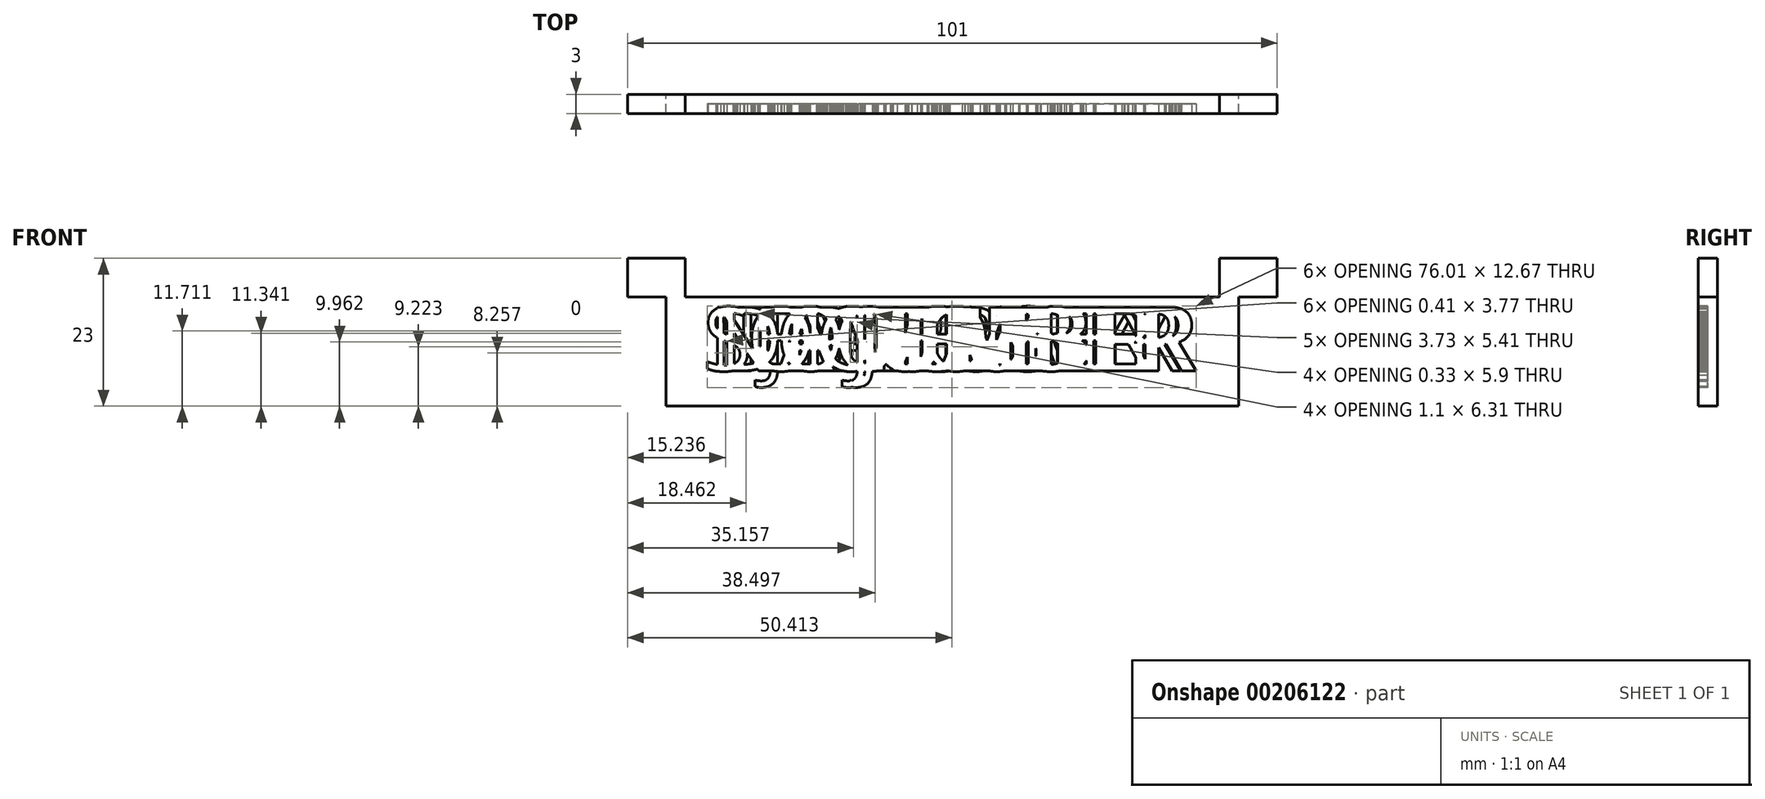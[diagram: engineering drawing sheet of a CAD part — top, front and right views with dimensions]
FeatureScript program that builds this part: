
annotation { "Feature Type Name" : "Feature", "Feature Type Description" : "" }
export const myFeature = defineFeature(function(context is Context, id is Id, definition is map)
    precondition{}
    {
        {
            var Q0;
            Q0=qCreatedBy(makeId("Front.planeOp"),FACE);
            var sketch = newSketch(context, id + "F0", { "sketchPlane" : qUnion([Q0])});
            skLineSegment(sketch, "E0.bottom", {"start": v(-51.5, 23) * mm, "end": v(-42.5, 23) * mm});
            skLineSegment(sketch, "E0.top", {"start": v(-45.5, 0) * mm, "end": v(43.5, 0) * mm});
            skLineSegment(sketch, "E0.left", {"start": v(-51.5, 23) * mm, "end": v(-51.5, 17) * mm});
            skLineSegment(sketch, "E0.right", {"start": v(49.5, 23) * mm, "end": v(49.5, 17) * mm});
            skLineSegment(sketch, "E1.top", {"start": v(-51.5, 17) * mm, "end": v(-45.5, 17) * mm});
            skLineSegment(sketch, "E1.right", {"start": v(-45.5, 0) * mm, "end": v(-45.5, 17) * mm});
            skLineSegment(sketch, "E2.bottom", {"start": v(-51.5, 23) * mm, "end": v(-42.5, 23) * mm, "construction": true});
            skLineSegment(sketch, "E2.top", {"start": v(-51.5, 17) * mm, "end": v(-42.5, 17) * mm, "construction": true});
            skLineSegment(sketch, "E2.left", {"start": v(-51.5, 23) * mm, "end": v(-51.5, 17) * mm, "construction": true});
            skLineSegment(sketch, "E2.right", {"start": v(-42.5, 23) * mm, "end": v(-42.5, 17) * mm, "construction": true});
            skLineSegment(sketch, "E3.top", {"start": v(-42.5, 17) * mm, "end": v(40.5, 17) * mm});
            skLineSegment(sketch, "E3.left", {"start": v(-42.5, 23) * mm, "end": v(-42.5, 17) * mm});
            skLineSegment(sketch, "E3.right", {"start": v(40.5, 23) * mm, "end": v(40.5, 17) * mm});
            skLineSegment(sketch, "E4.top", {"start": v(49.5, 17) * mm, "end": v(43.5, 17) * mm});
            skLineSegment(sketch, "E4.right", {"start": v(43.5, 0) * mm, "end": v(43.5, 17) * mm});
            skLineSegment(sketch, "E5.trimOffspring", {"start": v(40.5, 23) * mm, "end": v(49.5, 23) * mm});
            skSolve(sketch);
        }
        {
            var Q0;
            Q0=makeQuery(id+"F0.imprint","IMPRINT",FACE,{"disambiguationData":[TD([[makeQuery(id+"F0.imprint","IMPRINT",EDGE,{"derivedFrom":sQuery(id+"F0.wireOp",EDGE,"E0.bottom")}),-1.0]])]});
            extrude(context, id + "F1", {"entities" : qUnion([Q0]), "depth" : 3 * mm});
        }
        {
            var Q0;
            Q0=makeQuery(id+"F1.opExtrude","CAP_FACE",FACE,{"disambiguationData":[OSD([sQuery(id+"F0.wireOp",EDGE,"E0.bottom"),sQuery(id+"F0.wireOp",EDGE,"E0.top"),sQuery(id+"F0.wireOp",EDGE,"E0.left"),sQuery(id+"F0.wireOp",EDGE,"E0.right"),sQuery(id+"F0.wireOp",EDGE,"E1.top"),sQuery(id+"F0.wireOp",EDGE,"E1.right"),sQuery(id+"F0.wireOp",EDGE,"E3.top"),sQuery(id+"F0.wireOp",EDGE,"E3.left"),sQuery(id+"F0.wireOp",EDGE,"E3.right"),sQuery(id+"F0.wireOp",EDGE,"E4.top"),sQuery(id+"F0.wireOp",EDGE,"E4.right"),sQuery(id+"F0.wireOp",EDGE,"E5.trimOffspring")])],"isStart":false});
            var sketch = newSketch(context, id + "F2", { "sketchPlane" : qUnion([Q0])});
            skLineSegment(sketch, "E6.0", {"start": v(-45.5, 3.5) * mm, "end": v(-42, 3.5) * mm, "construction": true});
            skLineSegment(sketch, "E7.0", {"start": v(-42, 15.5) * mm, "end": v(40, 15.5) * mm, "construction": true});
            skLineSegment(sketch, "E8.0", {"start": v(-42, 0) * mm, "end": v(-42, 15.5) * mm, "construction": true});
            skText(sketch, "E9", { "text": "JANUARY", "fontName": "OpenSans-Regular.ttf"});
            skLineSegment(sketch, "E10.top", {"start": v(-45.5, 0) * mm, "end": v(-42, 0) * mm, "construction": true});
            skLineSegment(sketch, "E10.left", {"start": v(-45.5, 3.5) * mm, "end": v(-45.5, 0) * mm, "construction": true});
            skLineSegment(sketch, "E10.right", {"start": v(-42, 3.5) * mm, "end": v(-42, 0) * mm, "construction": true});
            skLineSegment(sketch, "E11.0", {"start": v(40, 0) * mm, "end": v(40, 17) * mm, "construction": true});
            skPoint(sketch, "E12.orphan", {"position": v(40, 15.5) * mm});
            skPoint(sketch, "E13.end.orphan", {"position": v(-1, 0) * mm});
            skLineSegment(sketch, "E14", {"start": v(-1, 17) * mm, "end": v(-1, 0) * mm, "construction": true});
            const initialGuessF2  = {"E9": [-0.0306, 0.0055, 1, 0, 0.01]};
            skSetInitialGuess(sketch, initialGuessF2);
            skSolve(sketch);
        }
        {
            var Q0;
            Q0=makeQuery(id+"F2.imprint","IMPRINT",FACE,{"disambiguationData":[TD([[makeQuery(id+"F2.imprint","IMPRINT",EDGE,{"derivedFrom":sQuery(id+"F2.wireOp",EDGE,"E9.sketch_text.stroke-0")}),-1.0]])]});
            var Q1;
            Q1=makeQuery(id+"F2.imprint","IMPRINT",FACE,{"disambiguationData":[TD([[makeQuery(id+"F2.imprint","IMPRINT",EDGE,{"derivedFrom":sQuery(id+"F2.wireOp",EDGE,"E9.sketch_text.stroke-10")}),-1.0]])]});
            var Q2;
            Q2=makeQuery(id+"F2.imprint","IMPRINT",FACE,{"disambiguationData":[TD([[makeQuery(id+"F2.imprint","IMPRINT",EDGE,{"derivedFrom":sQuery(id+"F2.wireOp",EDGE,"E9.sketch_text.stroke-23")}),-1.0]])]});
            var Q3;
            Q3=makeQuery(id+"F2.imprint","IMPRINT",FACE,{"disambiguationData":[TD([[makeQuery(id+"F2.imprint","IMPRINT",EDGE,{"derivedFrom":sQuery(id+"F2.wireOp",EDGE,"E9.sketch_text.stroke-38")}),-1.0]])]});
            var Q4;
            Q4=makeQuery(id+"F2.imprint","IMPRINT",FACE,{"disambiguationData":[TD([[makeQuery(id+"F2.imprint","IMPRINT",EDGE,{"derivedFrom":sQuery(id+"F2.wireOp",EDGE,"E9.sketch_text.stroke-52")}),-1.0]])]});
            var Q5;
            Q5=makeQuery(id+"F2.imprint","IMPRINT",FACE,{"disambiguationData":[TD([[makeQuery(id+"F2.imprint","IMPRINT",EDGE,{"derivedFrom":sQuery(id+"F2.wireOp",EDGE,"E9.sketch_text.stroke-65")}),-1.0]])]});
            var Q6;
            Q6=makeQuery(id+"F2.imprint","IMPRINT",FACE,{"disambiguationData":[TD([[makeQuery(id+"F2.imprint","IMPRINT",EDGE,{"derivedFrom":sQuery(id+"F2.wireOp",EDGE,"E9.sketch_text.stroke-83")}),-1.0]])]});
            extrude(context, id + "F3", {"entities" : qUnion([Q0, Q1, Q2, Q3, Q4, Q5, Q6]), "operationType" : NewBodyOperationType.REMOVE, "oppositeDirection" : true, "depth" : 1.5 * mm});
        }
        {
            var Q0;
            Q0 = qSketchRegion(id + "F0", true);
            extrude(context, id + "F4", {"entities" : qUnion([Q0]), "depth" : 3 * mm});
        }
        {
            var Q0;
            Q0=makeQuery(id+"F4.opExtrude","CAP_FACE",FACE,{"disambiguationData":[OSD([sQuery(id+"F0.wireOp",EDGE,"E0.bottom"),sQuery(id+"F0.wireOp",EDGE,"E0.top"),sQuery(id+"F0.wireOp",EDGE,"E0.left"),sQuery(id+"F0.wireOp",EDGE,"E0.right"),sQuery(id+"F0.wireOp",EDGE,"E1.top"),sQuery(id+"F0.wireOp",EDGE,"E1.right"),sQuery(id+"F0.wireOp",EDGE,"E3.top"),sQuery(id+"F0.wireOp",EDGE,"E3.left"),sQuery(id+"F0.wireOp",EDGE,"E3.right"),sQuery(id+"F0.wireOp",EDGE,"E4.top"),sQuery(id+"F0.wireOp",EDGE,"E4.right"),sQuery(id+"F0.wireOp",EDGE,"E5.trimOffspring")])],"isStart":false});
            var sketch = newSketch(context, id + "F5", { "sketchPlane" : qUnion([Q0])});
            skText(sketch, "E15", { "text": "FEBRUARY", "fontName": "OpenSans-Regular.ttf"});
            skPoint(sketch, "E16.orphan", {"position": v(44.71, 15.5) * mm});
            skPoint(sketch, "E17.end.orphan", {"position": v(-0.5, 0) * mm});
            skPoint(sketch, "E18.orphan", {"position": v(-46.71, 15.5) * mm});
            skLineSegment(sketch, "E19.0", {"start": v(-43.5, 15.5) * mm, "end": v(41.5, 15.5) * mm, "construction": true});
            skPoint(sketch, "E20.start.orphan", {"position": v(-1, 17) * mm});
            const initialGuessF5  = {"E15": [-0.03482, 0.0055, 1, 0, 0.01]};
            skSetInitialGuess(sketch, initialGuessF5);
            skSolve(sketch);
        }
        {
            var Q0;
            Q0=makeQuery(id+"F5.imprint","IMPRINT",FACE,{"disambiguationData":[TD([[makeQuery(id+"F5.imprint","IMPRINT",EDGE,{"derivedFrom":sQuery(id+"F5.wireOp",EDGE,"E15.sketch_text.stroke-0")}),-1.0]])]});
            var Q1;
            Q1=makeQuery(id+"F5.imprint","IMPRINT",FACE,{"disambiguationData":[TD([[makeQuery(id+"F5.imprint","IMPRINT",EDGE,{"derivedFrom":sQuery(id+"F5.wireOp",EDGE,"E15.sketch_text.stroke-10")}),-1.0]])]});
            var Q2;
            Q2=makeQuery(id+"F5.imprint","IMPRINT",FACE,{"disambiguationData":[TD([[makeQuery(id+"F5.imprint","IMPRINT",EDGE,{"derivedFrom":sQuery(id+"F5.wireOp",EDGE,"E15.sketch_text.stroke-22")}),-1.0]])]});
            var Q3;
            Q3=makeQuery(id+"F5.imprint","IMPRINT",FACE,{"disambiguationData":[TD([[makeQuery(id+"F5.imprint","IMPRINT",EDGE,{"derivedFrom":sQuery(id+"F5.wireOp",EDGE,"E15.sketch_text.stroke-47")}),-1.0]])]});
            var Q4;
            Q4=makeQuery(id+"F5.imprint","IMPRINT",FACE,{"disambiguationData":[TD([[makeQuery(id+"F5.imprint","IMPRINT",EDGE,{"derivedFrom":sQuery(id+"F5.wireOp",EDGE,"E15.sketch_text.stroke-65")}),-1.0]])]});
            var Q5;
            Q5=makeQuery(id+"F5.imprint","IMPRINT",FACE,{"disambiguationData":[TD([[makeQuery(id+"F5.imprint","IMPRINT",EDGE,{"derivedFrom":sQuery(id+"F5.wireOp",EDGE,"E15.sketch_text.stroke-79")}),-1.0]])]});
            var Q6;
            Q6=makeQuery(id+"F5.imprint","IMPRINT",FACE,{"disambiguationData":[TD([[makeQuery(id+"F5.imprint","IMPRINT",EDGE,{"derivedFrom":sQuery(id+"F5.wireOp",EDGE,"E15.sketch_text.stroke-92")}),-1.0]])]});
            var Q7;
            Q7=makeQuery(id+"F5.imprint","IMPRINT",FACE,{"disambiguationData":[TD([[makeQuery(id+"F5.imprint","IMPRINT",EDGE,{"derivedFrom":sQuery(id+"F5.wireOp",EDGE,"E15.sketch_text.stroke-110")}),-1.0]])]});
            extrude(context, id + "F6", {"entities" : qUnion([Q0, Q1, Q2, Q3, Q4, Q5, Q6, Q7]), "operationType" : NewBodyOperationType.REMOVE, "oppositeDirection" : true, "depth" : 1.5 * mm});
        }
        {
            var Q0;
            Q0=makeQuery(id+"F0.imprint","IMPRINT",FACE,{"disambiguationData":[TD([[makeQuery(id+"F0.imprint","IMPRINT",EDGE,{"derivedFrom":sQuery(id+"F0.wireOp",EDGE,"E0.bottom")}),-1.0]])]});
            extrude(context, id + "F7", {"entities" : qUnion([Q0]), "depth" : 3 * mm});
        }
        {
            var Q0;
            Q0=makeQuery(id+"F7.opExtrude","CAP_FACE",FACE,{"disambiguationData":[OSD([sQuery(id+"F0.wireOp",EDGE,"E0.bottom"),sQuery(id+"F0.wireOp",EDGE,"E0.top"),sQuery(id+"F0.wireOp",EDGE,"E0.left"),sQuery(id+"F0.wireOp",EDGE,"E0.right"),sQuery(id+"F0.wireOp",EDGE,"E1.top"),sQuery(id+"F0.wireOp",EDGE,"E1.right"),sQuery(id+"F0.wireOp",EDGE,"E3.top"),sQuery(id+"F0.wireOp",EDGE,"E3.left"),sQuery(id+"F0.wireOp",EDGE,"E3.right"),sQuery(id+"F0.wireOp",EDGE,"E4.top"),sQuery(id+"F0.wireOp",EDGE,"E4.right"),sQuery(id+"F0.wireOp",EDGE,"E5.trimOffspring")])],"isStart":false});
            var sketch = newSketch(context, id + "F8", { "sketchPlane" : qUnion([Q0])});
            skText(sketch, "E21", { "text": "MARCH", "fontName": "OpenSans-Regular.ttf"});
            skPoint(sketch, "E22.orphan", {"position": v(34.63, 15.5) * mm});
            skPoint(sketch, "E23.end.orphan", {"position": v(0, -12.7) * mm});
            skPoint(sketch, "E24.orphan", {"position": v(-36.63, 15.5) * mm});
            skPoint(sketch, "E25.start.orphan", {"position": v(0, 4.3) * mm});
            skLineSegment(sketch, "E26.0", {"start": v(-43.5, 15.5) * mm, "end": v(41.5, 15.5) * mm, "construction": true});
            const initialGuessF8  = {"E21": [-0.02473, 0.0055, 1, 0, 0.01]};
            skSetInitialGuess(sketch, initialGuessF8);
            skSolve(sketch);
        }
        {
            var Q0;
            Q0=makeQuery(id+"F8.imprint","IMPRINT",FACE,{"disambiguationData":[TD([[makeQuery(id+"F8.imprint","IMPRINT",EDGE,{"derivedFrom":sQuery(id+"F8.wireOp",EDGE,"E21.sketch_text.stroke-0")}),-1.0]])]});
            var Q1;
            Q1=makeQuery(id+"F8.imprint","IMPRINT",FACE,{"disambiguationData":[TD([[makeQuery(id+"F8.imprint","IMPRINT",EDGE,{"derivedFrom":sQuery(id+"F8.wireOp",EDGE,"E21.sketch_text.stroke-18")}),-1.0]])]});
            var Q2;
            Q2=makeQuery(id+"F8.imprint","IMPRINT",FACE,{"disambiguationData":[TD([[makeQuery(id+"F8.imprint","IMPRINT",EDGE,{"derivedFrom":sQuery(id+"F8.wireOp",EDGE,"E21.sketch_text.stroke-31")}),-1.0]])]});
            var Q3;
            Q3=makeQuery(id+"F8.imprint","IMPRINT",FACE,{"disambiguationData":[TD([[makeQuery(id+"F8.imprint","IMPRINT",EDGE,{"derivedFrom":sQuery(id+"F8.wireOp",EDGE,"E21.sketch_text.stroke-49")}),-1.0]])]});
            var Q4;
            Q4=makeQuery(id+"F8.imprint","IMPRINT",FACE,{"disambiguationData":[TD([[makeQuery(id+"F8.imprint","IMPRINT",EDGE,{"derivedFrom":sQuery(id+"F8.wireOp",EDGE,"E21.sketch_text.stroke-64")}),-1.0]])]});
            extrude(context, id + "F9", {"entities" : qUnion([Q0, Q1, Q2, Q3, Q4]), "operationType" : NewBodyOperationType.REMOVE, "oppositeDirection" : true, "depth" : 1.5 * mm});
        }
        {
            var Q0;
            Q0=makeQuery(id+"F0.imprint","IMPRINT",FACE,{"disambiguationData":[TD([[makeQuery(id+"F0.imprint","IMPRINT",EDGE,{"derivedFrom":sQuery(id+"F0.wireOp",EDGE,"E0.bottom")}),-1.0]])]});
            extrude(context, id + "F10", {"entities" : qUnion([Q0]), "depth" : 3 * mm});
        }
        {
            var Q0;
            Q0=makeQuery(id+"F10.opExtrude","CAP_FACE",FACE,{"disambiguationData":[OSD([sQuery(id+"F0.wireOp",EDGE,"E0.bottom"),sQuery(id+"F0.wireOp",EDGE,"E0.top"),sQuery(id+"F0.wireOp",EDGE,"E0.left"),sQuery(id+"F0.wireOp",EDGE,"E0.right"),sQuery(id+"F0.wireOp",EDGE,"E1.top"),sQuery(id+"F0.wireOp",EDGE,"E1.right"),sQuery(id+"F0.wireOp",EDGE,"E3.top"),sQuery(id+"F0.wireOp",EDGE,"E3.left"),sQuery(id+"F0.wireOp",EDGE,"E3.right"),sQuery(id+"F0.wireOp",EDGE,"E4.top"),sQuery(id+"F0.wireOp",EDGE,"E4.right"),sQuery(id+"F0.wireOp",EDGE,"E5.trimOffspring")])],"isStart":false});
            var sketch = newSketch(context, id + "F11", { "sketchPlane" : qUnion([Q0])});
            skText(sketch, "E27", { "text": "APRIL", "fontName": "OpenSans-Regular.ttf"});
            skPoint(sketch, "E28.orphan", {"position": v(29.1, 15.5) * mm});
            skPoint(sketch, "E29.end.orphan", {"position": v(0.3, -20.32) * mm});
            skPoint(sketch, "E30.orphan", {"position": v(-31.1, 15.5) * mm});
            skPoint(sketch, "E31.start.orphan", {"position": v(0.3, -3.32) * mm});
            skLineSegment(sketch, "E32.0", {"start": v(-43.5, 15.5) * mm, "end": v(41.5, 15.5) * mm});
            const initialGuessF11  = {"E27": [-0.0192, 0.0055, 1, 0, 0.01]};
            skSetInitialGuess(sketch, initialGuessF11);
            skSolve(sketch);
        }
        {
            var Q0;
            Q0=makeQuery(id+"F11.imprint","IMPRINT",FACE,{"disambiguationData":[TD([[makeQuery(id+"F11.imprint","IMPRINT",EDGE,{"derivedFrom":sQuery(id+"F11.wireOp",EDGE,"E27.sketch_text.stroke-0")}),-1.0]])]});
            var Q1;
            Q1=makeQuery(id+"F11.imprint","IMPRINT",FACE,{"disambiguationData":[TD([[makeQuery(id+"F11.imprint","IMPRINT",EDGE,{"derivedFrom":sQuery(id+"F11.wireOp",EDGE,"E27.sketch_text.stroke-13")}),-1.0]])]});
            var Q2;
            Q2=makeQuery(id+"F11.imprint","IMPRINT",FACE,{"disambiguationData":[TD([[makeQuery(id+"F11.imprint","IMPRINT",EDGE,{"derivedFrom":sQuery(id+"F11.wireOp",EDGE,"E27.sketch_text.stroke-28")}),-1.0]])]});
            var Q3;
            Q3=makeQuery(id+"F11.imprint","IMPRINT",FACE,{"disambiguationData":[TD([[makeQuery(id+"F11.imprint","IMPRINT",EDGE,{"derivedFrom":sQuery(id+"F11.wireOp",EDGE,"E27.sketch_text.stroke-46")}),-1.0]])]});
            var Q4;
            Q4=makeQuery(id+"F11.imprint","IMPRINT",FACE,{"disambiguationData":[TD([[makeQuery(id+"F11.imprint","IMPRINT",EDGE,{"derivedFrom":sQuery(id+"F11.wireOp",EDGE,"E27.sketch_text.stroke-50")}),-1.0]])]});
            extrude(context, id + "F12", {"entities" : qUnion([Q0, Q1, Q2, Q3, Q4]), "operationType" : NewBodyOperationType.REMOVE, "oppositeDirection" : true, "depth" : 1.5 * mm});
        }
        {
            var Q0;
            Q0=makeQuery(id+"F0.imprint","IMPRINT",FACE,{"disambiguationData":[TD([[makeQuery(id+"F0.imprint","IMPRINT",EDGE,{"derivedFrom":sQuery(id+"F0.wireOp",EDGE,"E0.bottom")}),-1.0]])]});
            extrude(context, id + "F13", {"entities" : qUnion([Q0]), "depth" : 3 * mm});
        }
        {
            var Q0;
            Q0=makeQuery(id+"F13.opExtrude","CAP_FACE",FACE,{"disambiguationData":[OSD([sQuery(id+"F0.wireOp",EDGE,"E0.bottom"),sQuery(id+"F0.wireOp",EDGE,"E0.top"),sQuery(id+"F0.wireOp",EDGE,"E0.left"),sQuery(id+"F0.wireOp",EDGE,"E0.right"),sQuery(id+"F0.wireOp",EDGE,"E1.top"),sQuery(id+"F0.wireOp",EDGE,"E1.right"),sQuery(id+"F0.wireOp",EDGE,"E3.top"),sQuery(id+"F0.wireOp",EDGE,"E3.left"),sQuery(id+"F0.wireOp",EDGE,"E3.right"),sQuery(id+"F0.wireOp",EDGE,"E4.top"),sQuery(id+"F0.wireOp",EDGE,"E4.right"),sQuery(id+"F0.wireOp",EDGE,"E5.trimOffspring")])],"isStart":false});
            var sketch = newSketch(context, id + "F14", { "sketchPlane" : qUnion([Q0])});
            skText(sketch, "E33", { "text": "MAY", "fontName": "OpenSans-Regular.ttf"});
            skPoint(sketch, "E34.orphan", {"position": v(25.4, 15.5) * mm});
            skPoint(sketch, "E35.end.orphan", {"position": v(0.48, -24.9) * mm});
            skPoint(sketch, "E36.orphan", {"position": v(-27.4, 15.5) * mm});
            skPoint(sketch, "E37.start.orphan", {"position": v(0.48, -7.9) * mm});
            skLineSegment(sketch, "E38.0", {"start": v(-40.3, 15.5) * mm, "end": v(38.3, 15.5) * mm});
            skLineSegment(sketch, "E39.0", {"start": v(-43.5, 15.5) * mm, "end": v(41.5, 15.5) * mm});
            const initialGuessF14  = {"E33": [-0.0155, 0.0055, 1, 0, 0.01]};
            skSetInitialGuess(sketch, initialGuessF14);
            skSolve(sketch);
        }
        {
            var Q0;
            Q0=makeQuery(id+"F0.imprint","IMPRINT",FACE,{"disambiguationData":[TD([[makeQuery(id+"F0.imprint","IMPRINT",EDGE,{"derivedFrom":sQuery(id+"F0.wireOp",EDGE,"E0.bottom")}),-1.0]])]});
            extrude(context, id + "F15", {"entities" : qUnion([Q0]), "depth" : 3 * mm});
        }
        {
            var Q0;
            Q0=makeQuery(id+"F15.opExtrude","CAP_FACE",FACE,{"disambiguationData":[OSD([sQuery(id+"F0.wireOp",EDGE,"E0.bottom"),sQuery(id+"F0.wireOp",EDGE,"E0.top"),sQuery(id+"F0.wireOp",EDGE,"E0.left"),sQuery(id+"F0.wireOp",EDGE,"E0.right"),sQuery(id+"F0.wireOp",EDGE,"E1.top"),sQuery(id+"F0.wireOp",EDGE,"E1.right"),sQuery(id+"F0.wireOp",EDGE,"E3.top"),sQuery(id+"F0.wireOp",EDGE,"E3.left"),sQuery(id+"F0.wireOp",EDGE,"E3.right"),sQuery(id+"F0.wireOp",EDGE,"E4.top"),sQuery(id+"F0.wireOp",EDGE,"E4.right"),sQuery(id+"F0.wireOp",EDGE,"E5.trimOffspring")])],"isStart":false});
            var sketch = newSketch(context, id + "F16", { "sketchPlane" : qUnion([Q0])});
            skText(sketch, "E40", { "text": "JUNE", "fontName": "OpenSans-Regular.ttf"});
            skPoint(sketch, "E41.orphan", {"position": v(26.97, 15.5) * mm});
            skPoint(sketch, "E42.end.orphan", {"position": v(0.65, -29.76) * mm});
            skPoint(sketch, "E43.orphan", {"position": v(-28.97, 15.5) * mm});
            skPoint(sketch, "E44.start.orphan", {"position": v(0.65, -12.76) * mm});
            skLineSegment(sketch, "E45.0", {"start": v(-41.88, 15.5) * mm, "end": v(39.88, 15.5) * mm});
            skLineSegment(sketch, "E46.0", {"start": v(-45.58, 15.5) * mm, "end": v(43.58, 15.5) * mm});
            skLineSegment(sketch, "E47.0", {"start": v(-43.5, 15.5) * mm, "end": v(41.5, 15.5) * mm});
            const initialGuessF16  = {"E40": [-0.01708, 0.0055, 1, 0, 0.01]};
            skSetInitialGuess(sketch, initialGuessF16);
            skSolve(sketch);
        }
        {
            var Q0;
            Q0=makeQuery(id+"F0.imprint","IMPRINT",FACE,{"disambiguationData":[TD([[makeQuery(id+"F0.imprint","IMPRINT",EDGE,{"derivedFrom":sQuery(id+"F0.wireOp",EDGE,"E0.bottom")}),-1.0]])]});
            extrude(context, id + "F17", {"entities" : qUnion([Q0]), "depth" : 3 * mm});
        }
        {
            var Q0;
            Q0=makeQuery(id+"F17.opExtrude","CAP_FACE",FACE,{"disambiguationData":[OSD([sQuery(id+"F0.wireOp",EDGE,"E0.bottom"),sQuery(id+"F0.wireOp",EDGE,"E0.top"),sQuery(id+"F0.wireOp",EDGE,"E0.left"),sQuery(id+"F0.wireOp",EDGE,"E0.right"),sQuery(id+"F0.wireOp",EDGE,"E1.top"),sQuery(id+"F0.wireOp",EDGE,"E1.right"),sQuery(id+"F0.wireOp",EDGE,"E3.top"),sQuery(id+"F0.wireOp",EDGE,"E3.left"),sQuery(id+"F0.wireOp",EDGE,"E3.right"),sQuery(id+"F0.wireOp",EDGE,"E4.top"),sQuery(id+"F0.wireOp",EDGE,"E4.right"),sQuery(id+"F0.wireOp",EDGE,"E5.trimOffspring")])],"isStart":false});
            var sketch = newSketch(context, id + "F18", { "sketchPlane" : qUnion([Q0])});
            skText(sketch, "E48", { "text": "JULY", "fontName": "OpenSans-Regular.ttf"});
            skPoint(sketch, "E49.orphan", {"position": v(25.79, 15.5) * mm});
            skPoint(sketch, "E50.end.orphan", {"position": v(0.82, -34.76) * mm});
            skPoint(sketch, "E51.orphan", {"position": v(-27.79, 15.5) * mm});
            skPoint(sketch, "E52.start.orphan", {"position": v(0.82, -17.76) * mm});
            skLineSegment(sketch, "E53.0", {"start": v(-40.7, 15.5) * mm, "end": v(38.7, 15.5) * mm});
            skLineSegment(sketch, "E54.0", {"start": v(-44.4, 15.5) * mm, "end": v(42.4, 15.5) * mm});
            skLineSegment(sketch, "E55.0", {"start": v(-42.81, 15.5) * mm, "end": v(40.81, 15.5) * mm});
            skLineSegment(sketch, "E56.0", {"start": v(-43.5, 15.5) * mm, "end": v(41.5, 15.5) * mm});
            const initialGuessF18  = {"E48": [-0.0159, 0.0055, 1, 0, 0.01]};
            skSetInitialGuess(sketch, initialGuessF18);
            skSolve(sketch);
        }
        {
            var Q0;
            Q0=makeQuery(id+"F0.imprint","IMPRINT",FACE,{"disambiguationData":[TD([[makeQuery(id+"F0.imprint","IMPRINT",EDGE,{"derivedFrom":sQuery(id+"F0.wireOp",EDGE,"E0.bottom")}),-1.0]])]});
            extrude(context, id + "F19", {"entities" : qUnion([Q0]), "depth" : 3 * mm});
        }
        {
            var Q0;
            Q0=makeQuery(id+"F19.opExtrude","CAP_FACE",FACE,{"disambiguationData":[OSD([sQuery(id+"F0.wireOp",EDGE,"E0.bottom"),sQuery(id+"F0.wireOp",EDGE,"E0.top"),sQuery(id+"F0.wireOp",EDGE,"E0.left"),sQuery(id+"F0.wireOp",EDGE,"E0.right"),sQuery(id+"F0.wireOp",EDGE,"E1.top"),sQuery(id+"F0.wireOp",EDGE,"E1.right"),sQuery(id+"F0.wireOp",EDGE,"E3.top"),sQuery(id+"F0.wireOp",EDGE,"E3.left"),sQuery(id+"F0.wireOp",EDGE,"E3.right"),sQuery(id+"F0.wireOp",EDGE,"E4.top"),sQuery(id+"F0.wireOp",EDGE,"E4.right"),sQuery(id+"F0.wireOp",EDGE,"E5.trimOffspring")])],"isStart":false});
            var sketch = newSketch(context, id + "F20", { "sketchPlane" : qUnion([Q0])});
            skText(sketch, "E57", { "text": "AUGUST", "fontName": "OpenSans-Regular.ttf"});
            skPoint(sketch, "E58.orphan", {"position": v(38, 15.5) * mm});
            skPoint(sketch, "E59.end.orphan", {"position": v(1, -39.82) * mm});
            skPoint(sketch, "E60.orphan", {"position": v(-40, 15.5) * mm});
            skPoint(sketch, "E61.start.orphan", {"position": v(1, -22.82) * mm});
            skLineSegment(sketch, "E62.0", {"start": v(-52.9, 15.5) * mm, "end": v(50.9, 15.5) * mm});
            skLineSegment(sketch, "E63.0", {"start": v(-56.6, 15.5) * mm, "end": v(54.6, 15.5) * mm});
            skLineSegment(sketch, "E64.0", {"start": v(-55.02, 15.5) * mm, "end": v(53.02, 15.5) * mm});
            skLineSegment(sketch, "E65.0", {"start": v(-56.2, 15.5) * mm, "end": v(54.2, 15.5) * mm});
            skLineSegment(sketch, "E66.0", {"start": v(-43.5, 15.5) * mm, "end": v(41.5, 15.5) * mm});
            const initialGuessF20  = {"E57": [-0.0281, 0.0055, 1, 0, 0.01]};
            skSetInitialGuess(sketch, initialGuessF20);
            skSolve(sketch);
        }
        {
            var Q0;
            Q0=makeQuery(id+"F0.imprint","IMPRINT",FACE,{"disambiguationData":[TD([[makeQuery(id+"F0.imprint","IMPRINT",EDGE,{"derivedFrom":sQuery(id+"F0.wireOp",EDGE,"E0.bottom")}),-1.0]])]});
            extrude(context, id + "F21", {"entities" : qUnion([Q0]), "depth" : 3 * mm});
        }
        {
            var Q0;
            Q0=makeQuery(id+"F21.opExtrude","CAP_FACE",FACE,{"disambiguationData":[OSD([sQuery(id+"F0.wireOp",EDGE,"E0.bottom"),sQuery(id+"F0.wireOp",EDGE,"E0.top"),sQuery(id+"F0.wireOp",EDGE,"E0.left"),sQuery(id+"F0.wireOp",EDGE,"E0.right"),sQuery(id+"F0.wireOp",EDGE,"E1.top"),sQuery(id+"F0.wireOp",EDGE,"E1.right"),sQuery(id+"F0.wireOp",EDGE,"E3.top"),sQuery(id+"F0.wireOp",EDGE,"E3.left"),sQuery(id+"F0.wireOp",EDGE,"E3.right"),sQuery(id+"F0.wireOp",EDGE,"E4.top"),sQuery(id+"F0.wireOp",EDGE,"E4.right"),sQuery(id+"F0.wireOp",EDGE,"E5.trimOffspring")])],"isStart":false});
            var sketch = newSketch(context, id + "F22", { "sketchPlane" : qUnion([Q0])});
            skText(sketch, "E67", { "text": "SEPTEMBER", "fontName": "OpenSans-Regular.ttf"});
            skPoint(sketch, "E68.orphan", {"position": v(49.2, 15.5) * mm});
            skPoint(sketch, "E69.end.orphan", {"position": v(1.16, -44.91) * mm});
            skPoint(sketch, "E70.orphan", {"position": v(-51.2, 15.5) * mm});
            skPoint(sketch, "E71.start.orphan", {"position": v(1.16, -27.91) * mm});
            const initialGuessF22  = {"E67": [-0.03981, 0.0055, 1, 0, 0.01]};
            skSetInitialGuess(sketch, initialGuessF22);
            skSolve(sketch);
        }
        {
            var Q0;
            Q0=makeQuery(id+"F0.imprint","IMPRINT",FACE,{"disambiguationData":[TD([[makeQuery(id+"F0.imprint","IMPRINT",EDGE,{"derivedFrom":sQuery(id+"F0.wireOp",EDGE,"E0.bottom")}),-1.0]])]});
            extrude(context, id + "F23", {"entities" : qUnion([Q0]), "depth" : 3 * mm});
        }
        {
            var Q0;
            Q0=makeQuery(id+"F23.opExtrude","CAP_FACE",FACE,{"disambiguationData":[OSD([sQuery(id+"F0.wireOp",EDGE,"E0.bottom"),sQuery(id+"F0.wireOp",EDGE,"E0.top"),sQuery(id+"F0.wireOp",EDGE,"E0.left"),sQuery(id+"F0.wireOp",EDGE,"E0.right"),sQuery(id+"F0.wireOp",EDGE,"E1.top"),sQuery(id+"F0.wireOp",EDGE,"E1.right"),sQuery(id+"F0.wireOp",EDGE,"E3.top"),sQuery(id+"F0.wireOp",EDGE,"E3.left"),sQuery(id+"F0.wireOp",EDGE,"E3.right"),sQuery(id+"F0.wireOp",EDGE,"E4.top"),sQuery(id+"F0.wireOp",EDGE,"E4.right"),sQuery(id+"F0.wireOp",EDGE,"E5.trimOffspring")])],"isStart":false});
            var sketch = newSketch(context, id + "F24", { "sketchPlane" : qUnion([Q0])});
            skText(sketch, "E72", { "text": "OCTOBER", "fontName": "OpenSans-Regular.ttf"});
            skPoint(sketch, "E73.orphan", {"position": v(42.42, 15.5) * mm});
            skPoint(sketch, "E74.end.orphan", {"position": v(1.08, -34.46) * mm});
            skPoint(sketch, "E75.orphan", {"position": v(-44.42, 15.5) * mm});
            skPoint(sketch, "E76.start.orphan", {"position": v(1.08, -17.46) * mm});
            skLineSegment(sketch, "E77.0", {"start": v(-42.5, 15.5) * mm, "end": v(40.5, 15.5) * mm});
            const initialGuessF24  = {"E72": [-0.03303, 0.0055, 1, 0, 0.01]};
            skSetInitialGuess(sketch, initialGuessF24);
            skSolve(sketch);
        }
        {
            var Q0;
            Q0=makeQuery(id+"F0.imprint","IMPRINT",FACE,{"disambiguationData":[TD([[makeQuery(id+"F0.imprint","IMPRINT",EDGE,{"derivedFrom":sQuery(id+"F0.wireOp",EDGE,"E0.bottom")}),-1.0]])]});
            extrude(context, id + "F25", {"entities" : qUnion([Q0]), "depth" : 3 * mm});
        }
        {
            var Q0;
            Q0=makeQuery(id+"F25.opExtrude","CAP_FACE",FACE,{"disambiguationData":[OSD([sQuery(id+"F0.wireOp",EDGE,"E0.bottom"),sQuery(id+"F0.wireOp",EDGE,"E0.top"),sQuery(id+"F0.wireOp",EDGE,"E0.left"),sQuery(id+"F0.wireOp",EDGE,"E0.right"),sQuery(id+"F0.wireOp",EDGE,"E1.top"),sQuery(id+"F0.wireOp",EDGE,"E1.right"),sQuery(id+"F0.wireOp",EDGE,"E3.top"),sQuery(id+"F0.wireOp",EDGE,"E3.left"),sQuery(id+"F0.wireOp",EDGE,"E3.right"),sQuery(id+"F0.wireOp",EDGE,"E4.top"),sQuery(id+"F0.wireOp",EDGE,"E4.right"),sQuery(id+"F0.wireOp",EDGE,"E5.trimOffspring")])],"isStart":false});
            var sketch = newSketch(context, id + "F26", { "sketchPlane" : qUnion([Q0])});
            skText(sketch, "E78", { "text": "NOVEMBER", "fontName": "OpenSans-Regular.ttf"});
            skPoint(sketch, "E79.orphan", {"position": v(48.29, 15.5) * mm});
            skPoint(sketch, "E80.end.orphan", {"position": v(1.08, -34.46) * mm});
            skPoint(sketch, "E81.orphan", {"position": v(-50.29, 15.5) * mm});
            skPoint(sketch, "E82.start.orphan", {"position": v(1.08, -17.46) * mm});
            skLineSegment(sketch, "E83.0", {"start": v(-42.5, 15.5) * mm, "end": v(40.5, 15.5) * mm});
            const initialGuessF26  = {"E78": [-0.0389, 0.0055, 1, 0, 0.01]};
            skSetInitialGuess(sketch, initialGuessF26);
            skSolve(sketch);
        }
        {
            var Q0;
            Q0=makeQuery(id+"F0.imprint","IMPRINT",FACE,{"disambiguationData":[TD([[makeQuery(id+"F0.imprint","IMPRINT",EDGE,{"derivedFrom":sQuery(id+"F0.wireOp",EDGE,"E0.bottom")}),-1.0]])]});
            extrude(context, id + "F27", {"entities" : qUnion([Q0]), "depth" : 3 * mm});
        }
        {
            var Q0;
            Q0=makeQuery(id+"F27.opExtrude","CAP_FACE",FACE,{"disambiguationData":[OSD([sQuery(id+"F0.wireOp",EDGE,"E0.bottom"),sQuery(id+"F0.wireOp",EDGE,"E0.top"),sQuery(id+"F0.wireOp",EDGE,"E0.left"),sQuery(id+"F0.wireOp",EDGE,"E0.right"),sQuery(id+"F0.wireOp",EDGE,"E1.top"),sQuery(id+"F0.wireOp",EDGE,"E1.right"),sQuery(id+"F0.wireOp",EDGE,"E3.top"),sQuery(id+"F0.wireOp",EDGE,"E3.left"),sQuery(id+"F0.wireOp",EDGE,"E3.right"),sQuery(id+"F0.wireOp",EDGE,"E4.top"),sQuery(id+"F0.wireOp",EDGE,"E4.right"),sQuery(id+"F0.wireOp",EDGE,"E5.trimOffspring")])],"isStart":false});
            var sketch = newSketch(context, id + "F28", { "sketchPlane" : qUnion([Q0])});
            skText(sketch, "E84", { "text": "DECEMBER", "fontName": "OpenSans-Regular.ttf"});
            skPoint(sketch, "E85.orphan", {"position": v(46.82, 15.5) * mm});
            skPoint(sketch, "E86.end.orphan", {"position": v(1.08, -34.46) * mm});
            skPoint(sketch, "E87.orphan", {"position": v(-48.82, 15.5) * mm});
            skPoint(sketch, "E88.start.orphan", {"position": v(1.08, -17.46) * mm});
            skLineSegment(sketch, "E89.0", {"start": v(-42.5, 15.5) * mm, "end": v(40.5, 15.5) * mm});
            const initialGuessF28  = {"E84": [-0.03742, 0.0055, 1, 0, 0.01]};
            skSetInitialGuess(sketch, initialGuessF28);
            skSolve(sketch);
        }
        {
            var Q0;
            Q0=makeQuery(id+"F28.imprint","IMPRINT",FACE,{"disambiguationData":[TD([[makeQuery(id+"F28.imprint","IMPRINT",EDGE,{"derivedFrom":sQuery(id+"F28.wireOp",EDGE,"E84.sketch_text.stroke-0")}),-1.0]])]});
            var Q1;
            Q1=makeQuery(id+"F28.imprint","IMPRINT",FACE,{"disambiguationData":[TD([[makeQuery(id+"F28.imprint","IMPRINT",EDGE,{"derivedFrom":sQuery(id+"F28.wireOp",EDGE,"E84.sketch_text.stroke-14")}),-1.0]])]});
            var Q2;
            Q2=makeQuery(id+"F28.imprint","IMPRINT",FACE,{"disambiguationData":[TD([[makeQuery(id+"F28.imprint","IMPRINT",EDGE,{"derivedFrom":sQuery(id+"F28.wireOp",EDGE,"E84.sketch_text.stroke-26")}),-1.0]])]});
            var Q3;
            Q3=makeQuery(id+"F28.imprint","IMPRINT",FACE,{"disambiguationData":[TD([[makeQuery(id+"F28.imprint","IMPRINT",EDGE,{"derivedFrom":sQuery(id+"F28.wireOp",EDGE,"E84.sketch_text.stroke-41")}),-1.0]])]});
            var Q4;
            Q4=makeQuery(id+"F28.imprint","IMPRINT",FACE,{"disambiguationData":[TD([[makeQuery(id+"F28.imprint","IMPRINT",EDGE,{"derivedFrom":sQuery(id+"F28.wireOp",EDGE,"E84.sketch_text.stroke-53")}),-1.0]])]});
            var Q5;
            Q5=makeQuery(id+"F28.imprint","IMPRINT",FACE,{"disambiguationData":[TD([[makeQuery(id+"F28.imprint","IMPRINT",EDGE,{"derivedFrom":sQuery(id+"F28.wireOp",EDGE,"E84.sketch_text.stroke-71")}),-1.0]])]});
            var Q6;
            Q6=makeQuery(id+"F28.imprint","IMPRINT",FACE,{"disambiguationData":[TD([[makeQuery(id+"F28.imprint","IMPRINT",EDGE,{"derivedFrom":sQuery(id+"F28.wireOp",EDGE,"E84.sketch_text.stroke-96")}),-1.0]])]});
            var Q7;
            Q7=makeQuery(id+"F28.imprint","IMPRINT",FACE,{"disambiguationData":[TD([[makeQuery(id+"F28.imprint","IMPRINT",EDGE,{"derivedFrom":sQuery(id+"F28.wireOp",EDGE,"E84.sketch_text.stroke-108")}),-1.0]])]});
            extrude(context, id + "F29", {"entities" : qUnion([Q0, Q1, Q2, Q3, Q4, Q5, Q6, Q7]), "operationType" : NewBodyOperationType.REMOVE, "oppositeDirection" : true, "depth" : 1.5 * mm});
        }
        {
            var Q0;
            Q0=makeQuery(id+"F26.imprint","IMPRINT",FACE,{"disambiguationData":[TD([[makeQuery(id+"F26.imprint","IMPRINT",EDGE,{"derivedFrom":sQuery(id+"F26.wireOp",EDGE,"E78.sketch_text.stroke-0")}),-1.0]])]});
            var Q1;
            Q1=makeQuery(id+"F26.imprint","IMPRINT",FACE,{"disambiguationData":[TD([[makeQuery(id+"F26.imprint","IMPRINT",EDGE,{"derivedFrom":sQuery(id+"F26.wireOp",EDGE,"E78.sketch_text.stroke-15")}),-1.0]])]});
            var Q2;
            Q2=makeQuery(id+"F26.imprint","IMPRINT",FACE,{"disambiguationData":[TD([[makeQuery(id+"F26.imprint","IMPRINT",EDGE,{"derivedFrom":sQuery(id+"F26.wireOp",EDGE,"E78.sketch_text.stroke-31")}),-1.0]])]});
            var Q3;
            Q3=makeQuery(id+"F26.imprint","IMPRINT",FACE,{"disambiguationData":[TD([[makeQuery(id+"F26.imprint","IMPRINT",EDGE,{"derivedFrom":sQuery(id+"F26.wireOp",EDGE,"E78.sketch_text.stroke-40")}),-1.0]])]});
            var Q4;
            Q4=makeQuery(id+"F26.imprint","IMPRINT",FACE,{"disambiguationData":[TD([[makeQuery(id+"F26.imprint","IMPRINT",EDGE,{"derivedFrom":sQuery(id+"F26.wireOp",EDGE,"E78.sketch_text.stroke-52")}),-1.0]])]});
            var Q5;
            Q5=makeQuery(id+"F26.imprint","IMPRINT",FACE,{"disambiguationData":[TD([[makeQuery(id+"F26.imprint","IMPRINT",EDGE,{"derivedFrom":sQuery(id+"F26.wireOp",EDGE,"E78.sketch_text.stroke-70")}),-1.0]])]});
            var Q6;
            Q6=makeQuery(id+"F26.imprint","IMPRINT",FACE,{"disambiguationData":[TD([[makeQuery(id+"F26.imprint","IMPRINT",EDGE,{"derivedFrom":sQuery(id+"F26.wireOp",EDGE,"E78.sketch_text.stroke-95")}),-1.0]])]});
            var Q7;
            Q7=makeQuery(id+"F26.imprint","IMPRINT",FACE,{"disambiguationData":[TD([[makeQuery(id+"F26.imprint","IMPRINT",EDGE,{"derivedFrom":sQuery(id+"F26.wireOp",EDGE,"E78.sketch_text.stroke-107")}),-1.0]])]});
            extrude(context, id + "F30", {"entities" : qUnion([Q0, Q1, Q2, Q3, Q4, Q5, Q6, Q7]), "operationType" : NewBodyOperationType.REMOVE, "oppositeDirection" : true, "depth" : 1.5 * mm});
        }
        {
            var Q0;
            Q0=makeQuery(id+"F24.imprint","IMPRINT",FACE,{"disambiguationData":[TD([[makeQuery(id+"F24.imprint","IMPRINT",EDGE,{"derivedFrom":sQuery(id+"F24.wireOp",EDGE,"E72.sketch_text.stroke-0")}),-1.0]])]});
            var Q1;
            Q1=makeQuery(id+"F24.imprint","IMPRINT",FACE,{"disambiguationData":[TD([[makeQuery(id+"F24.imprint","IMPRINT",EDGE,{"derivedFrom":sQuery(id+"F24.wireOp",EDGE,"E72.sketch_text.stroke-16")}),-1.0]])]});
            var Q2;
            Q2=makeQuery(id+"F24.imprint","IMPRINT",FACE,{"disambiguationData":[TD([[makeQuery(id+"F24.imprint","IMPRINT",EDGE,{"derivedFrom":sQuery(id+"F24.wireOp",EDGE,"E72.sketch_text.stroke-31")}),-1.0]])]});
            var Q3;
            Q3=makeQuery(id+"F24.imprint","IMPRINT",FACE,{"disambiguationData":[TD([[makeQuery(id+"F24.imprint","IMPRINT",EDGE,{"derivedFrom":sQuery(id+"F24.wireOp",EDGE,"E72.sketch_text.stroke-39")}),-1.0]])]});
            var Q4;
            Q4=makeQuery(id+"F24.imprint","IMPRINT",FACE,{"disambiguationData":[TD([[makeQuery(id+"F24.imprint","IMPRINT",EDGE,{"derivedFrom":sQuery(id+"F24.wireOp",EDGE,"E72.sketch_text.stroke-55")}),-1.0]])]});
            var Q5;
            Q5=makeQuery(id+"F24.imprint","IMPRINT",FACE,{"disambiguationData":[TD([[makeQuery(id+"F24.imprint","IMPRINT",EDGE,{"derivedFrom":sQuery(id+"F24.wireOp",EDGE,"E72.sketch_text.stroke-80")}),-1.0]])]});
            var Q6;
            Q6=makeQuery(id+"F24.imprint","IMPRINT",FACE,{"disambiguationData":[TD([[makeQuery(id+"F24.imprint","IMPRINT",EDGE,{"derivedFrom":sQuery(id+"F24.wireOp",EDGE,"E72.sketch_text.stroke-92")}),-1.0]])]});
            extrude(context, id + "F31", {"entities" : qUnion([Q0, Q1, Q2, Q3, Q4, Q5, Q6]), "operationType" : NewBodyOperationType.REMOVE, "oppositeDirection" : true, "depth" : 1.5 * mm});
        }
        {
            var Q0;
            Q0=makeQuery(id+"F22.imprint","IMPRINT",FACE,{"disambiguationData":[TD([[makeQuery(id+"F22.imprint","IMPRINT",EDGE,{"derivedFrom":sQuery(id+"F22.wireOp",EDGE,"E67.sketch_text.stroke-0")}),-1.0]])]});
            var Q1;
            Q1=makeQuery(id+"F22.imprint","IMPRINT",FACE,{"disambiguationData":[TD([[makeQuery(id+"F22.imprint","IMPRINT",EDGE,{"derivedFrom":sQuery(id+"F22.wireOp",EDGE,"E67.sketch_text.stroke-25")}),-1.0]])]});
            var Q2;
            Q2=makeQuery(id+"F22.imprint","IMPRINT",FACE,{"disambiguationData":[TD([[makeQuery(id+"F22.imprint","IMPRINT",EDGE,{"derivedFrom":sQuery(id+"F22.wireOp",EDGE,"E67.sketch_text.stroke-37")}),-1.0]])]});
            var Q3;
            Q3=makeQuery(id+"F22.imprint","IMPRINT",FACE,{"disambiguationData":[TD([[makeQuery(id+"F22.imprint","IMPRINT",EDGE,{"derivedFrom":sQuery(id+"F22.wireOp",EDGE,"E67.sketch_text.stroke-52")}),-1.0]])]});
            var Q4;
            Q4=makeQuery(id+"F22.imprint","IMPRINT",FACE,{"disambiguationData":[TD([[makeQuery(id+"F22.imprint","IMPRINT",EDGE,{"derivedFrom":sQuery(id+"F22.wireOp",EDGE,"E67.sketch_text.stroke-60")}),-1.0]])]});
            var Q5;
            Q5=makeQuery(id+"F22.imprint","IMPRINT",FACE,{"disambiguationData":[TD([[makeQuery(id+"F22.imprint","IMPRINT",EDGE,{"derivedFrom":sQuery(id+"F22.wireOp",EDGE,"E67.sketch_text.stroke-72")}),-1.0]])]});
            var Q6;
            Q6=makeQuery(id+"F22.imprint","IMPRINT",FACE,{"disambiguationData":[TD([[makeQuery(id+"F22.imprint","IMPRINT",EDGE,{"derivedFrom":sQuery(id+"F22.wireOp",EDGE,"E67.sketch_text.stroke-90")}),-1.0]])]});
            var Q7;
            Q7=makeQuery(id+"F22.imprint","IMPRINT",FACE,{"disambiguationData":[TD([[makeQuery(id+"F22.imprint","IMPRINT",EDGE,{"derivedFrom":sQuery(id+"F22.wireOp",EDGE,"E67.sketch_text.stroke-115")}),-1.0]])]});
            var Q8;
            Q8=makeQuery(id+"F22.imprint","IMPRINT",FACE,{"disambiguationData":[TD([[makeQuery(id+"F22.imprint","IMPRINT",EDGE,{"derivedFrom":sQuery(id+"F22.wireOp",EDGE,"E67.sketch_text.stroke-127")}),-1.0]])]});
            extrude(context, id + "F32", {"entities" : qUnion([Q0, Q1, Q2, Q3, Q4, Q5, Q6, Q7, Q8]), "operationType" : NewBodyOperationType.REMOVE, "oppositeDirection" : true, "depth" : 1.5 * mm});
        }
        {
            var Q0;
            Q0=makeQuery(id+"F20.imprint","IMPRINT",FACE,{"disambiguationData":[TD([[makeQuery(id+"F20.imprint","IMPRINT",EDGE,{"derivedFrom":sQuery(id+"F20.wireOp",EDGE,"E57.sketch_text.stroke-0")}),-1.0]])]});
            var Q1;
            Q1=makeQuery(id+"F20.imprint","IMPRINT",FACE,{"disambiguationData":[TD([[makeQuery(id+"F20.imprint","IMPRINT",EDGE,{"derivedFrom":sQuery(id+"F20.wireOp",EDGE,"E57.sketch_text.stroke-13")}),-1.0]])]});
            var Q2;
            Q2=makeQuery(id+"F20.imprint","IMPRINT",FACE,{"disambiguationData":[TD([[makeQuery(id+"F20.imprint","IMPRINT",EDGE,{"derivedFrom":sQuery(id+"F20.wireOp",EDGE,"E57.sketch_text.stroke-27")}),-1.0]])]});
            var Q3;
            Q3=makeQuery(id+"F20.imprint","IMPRINT",FACE,{"disambiguationData":[TD([[makeQuery(id+"F20.imprint","IMPRINT",EDGE,{"derivedFrom":sQuery(id+"F20.wireOp",EDGE,"E57.sketch_text.stroke-47")}),-1.0]])]});
            var Q4;
            Q4=makeQuery(id+"F20.imprint","IMPRINT",FACE,{"disambiguationData":[TD([[makeQuery(id+"F20.imprint","IMPRINT",EDGE,{"derivedFrom":sQuery(id+"F20.wireOp",EDGE,"E57.sketch_text.stroke-61")}),-1.0]])]});
            var Q5;
            Q5=makeQuery(id+"F20.imprint","IMPRINT",FACE,{"disambiguationData":[TD([[makeQuery(id+"F20.imprint","IMPRINT",EDGE,{"derivedFrom":sQuery(id+"F20.wireOp",EDGE,"E57.sketch_text.stroke-86")}),-1.0]])]});
            extrude(context, id + "F33", {"entities" : qUnion([Q0, Q1, Q2, Q3, Q4, Q5]), "operationType" : NewBodyOperationType.REMOVE, "oppositeDirection" : true, "depth" : 1.5 * mm});
        }
        {
            var Q0;
            Q0=makeQuery(id+"F18.imprint","IMPRINT",FACE,{"disambiguationData":[TD([[makeQuery(id+"F18.imprint","IMPRINT",EDGE,{"derivedFrom":sQuery(id+"F18.wireOp",EDGE,"E48.sketch_text.stroke-0")}),-1.0]])]});
            var Q1;
            Q1=makeQuery(id+"F18.imprint","IMPRINT",FACE,{"disambiguationData":[TD([[makeQuery(id+"F18.imprint","IMPRINT",EDGE,{"derivedFrom":sQuery(id+"F18.wireOp",EDGE,"E48.sketch_text.stroke-10")}),-1.0]])]});
            var Q2;
            Q2=makeQuery(id+"F18.imprint","IMPRINT",FACE,{"disambiguationData":[TD([[makeQuery(id+"F18.imprint","IMPRINT",EDGE,{"derivedFrom":sQuery(id+"F18.wireOp",EDGE,"E48.sketch_text.stroke-24")}),-1.0]])]});
            var Q3;
            Q3=makeQuery(id+"F18.imprint","IMPRINT",FACE,{"disambiguationData":[TD([[makeQuery(id+"F18.imprint","IMPRINT",EDGE,{"derivedFrom":sQuery(id+"F18.wireOp",EDGE,"E48.sketch_text.stroke-30")}),-1.0]])]});
            extrude(context, id + "F34", {"entities" : qUnion([Q0, Q1, Q2, Q3]), "operationType" : NewBodyOperationType.REMOVE, "oppositeDirection" : true, "depth" : 1.5 * mm});
        }
        {
            var Q0;
            Q0=makeQuery(id+"F16.imprint","IMPRINT",FACE,{"disambiguationData":[TD([[makeQuery(id+"F16.imprint","IMPRINT",EDGE,{"derivedFrom":sQuery(id+"F16.wireOp",EDGE,"E40.sketch_text.stroke-0")}),-1.0]])]});
            var Q1;
            Q1=makeQuery(id+"F16.imprint","IMPRINT",FACE,{"disambiguationData":[TD([[makeQuery(id+"F16.imprint","IMPRINT",EDGE,{"derivedFrom":sQuery(id+"F16.wireOp",EDGE,"E40.sketch_text.stroke-10")}),-1.0]])]});
            var Q2;
            Q2=makeQuery(id+"F16.imprint","IMPRINT",FACE,{"disambiguationData":[TD([[makeQuery(id+"F16.imprint","IMPRINT",EDGE,{"derivedFrom":sQuery(id+"F16.wireOp",EDGE,"E40.sketch_text.stroke-24")}),-1.0]])]});
            var Q3;
            Q3=makeQuery(id+"F16.imprint","IMPRINT",FACE,{"disambiguationData":[TD([[makeQuery(id+"F16.imprint","IMPRINT",EDGE,{"derivedFrom":sQuery(id+"F16.wireOp",EDGE,"E40.sketch_text.stroke-39")}),-1.0]])]});
            extrude(context, id + "F35", {"entities" : qUnion([Q0, Q1, Q2, Q3]), "operationType" : NewBodyOperationType.REMOVE, "oppositeDirection" : true, "depth" : 1.5 * mm});
        }
        {
            var Q0;
            Q0=makeQuery(id+"F14.imprint","IMPRINT",FACE,{"disambiguationData":[TD([[makeQuery(id+"F14.imprint","IMPRINT",EDGE,{"derivedFrom":sQuery(id+"F14.wireOp",EDGE,"E33.sketch_text.stroke-0")}),-1.0]])]});
            var Q1;
            Q1=makeQuery(id+"F14.imprint","IMPRINT",FACE,{"disambiguationData":[TD([[makeQuery(id+"F14.imprint","IMPRINT",EDGE,{"derivedFrom":sQuery(id+"F14.wireOp",EDGE,"E33.sketch_text.stroke-18")}),-1.0]])]});
            var Q2;
            Q2=makeQuery(id+"F14.imprint","IMPRINT",FACE,{"disambiguationData":[TD([[makeQuery(id+"F14.imprint","IMPRINT",EDGE,{"derivedFrom":sQuery(id+"F14.wireOp",EDGE,"E33.sketch_text.stroke-31")}),-1.0]])]});
            extrude(context, id + "F36", {"entities" : qUnion([Q0, Q1, Q2]), "operationType" : NewBodyOperationType.REMOVE, "oppositeDirection" : true, "depth" : 1.5 * mm});
        }
        {
            var Q0;
            Q0=makeQuery(id+"F0.imprint","IMPRINT",FACE,{"disambiguationData":[TD([[makeQuery(id+"F0.imprint","IMPRINT",EDGE,{"derivedFrom":sQuery(id+"F0.wireOp",EDGE,"E0.bottom")}),-1.0]])]});
            extrude(context, id + "F37", {"entities" : qUnion([Q0]), "depth" : 3 * mm});
        }
    });
